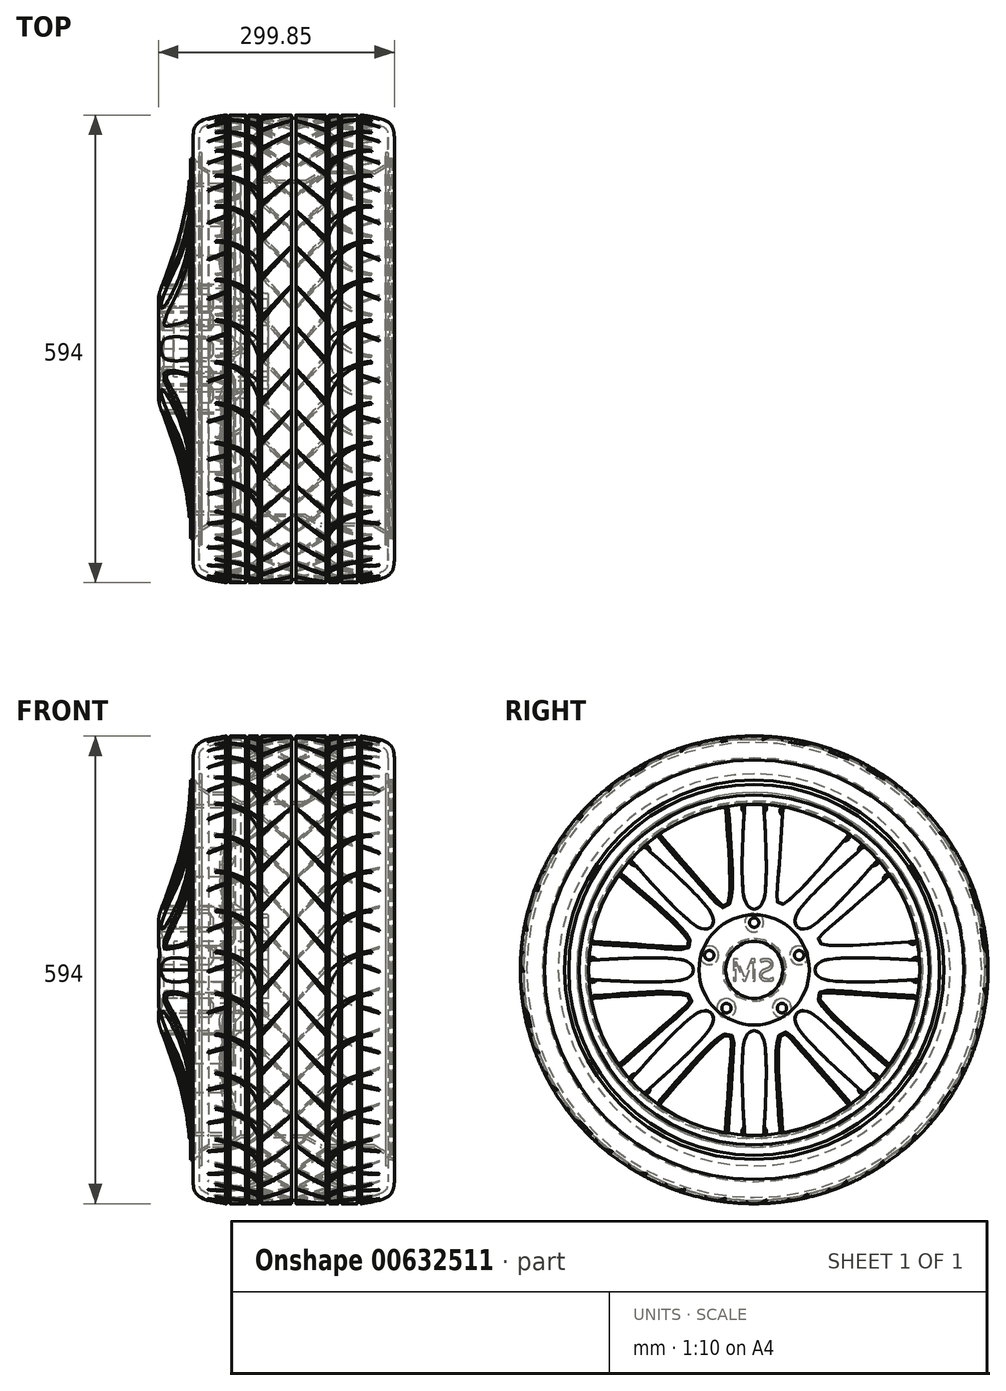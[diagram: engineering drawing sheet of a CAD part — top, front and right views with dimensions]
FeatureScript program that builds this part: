
annotation { "Feature Type Name" : "Feature", "Feature Type Description" : "" }
export const myFeature = defineFeature(function(context is Context, id is Id, definition is map)
    precondition{}
    {
        {
            var Q0;
            Q0=qCreatedBy(makeId("Front.planeOp"),FACE);
            var sketch = newSketch(context, id + "F0", { "sketchPlane" : qUnion([Q0])});
            skLineSegment(sketch, "E0", {"start": v(-128, 244.95) * mm, "end": v(-128, 266.43) * mm});
            skLineSegment(sketch, "E1", {"start": v(0, 297) * mm, "end": v(86.47, 297) * mm});
            skLineSegment(sketch, "E2", {"start": v(128, 266.43) * mm, "end": v(128, 244.95) * mm});
            skLineSegment(sketch, "E3", {"start": v(120, 249) * mm, "end": v(117, 249) * mm});
            skLineSegment(sketch, "E4", {"start": v(117, 249) * mm, "end": v(117, 241) * mm});
            skLineSegment(sketch, "E5", {"start": v(-120, 269) * mm, "end": v(-120, 249) * mm});
            skLineSegment(sketch, "E6", {"start": v(-120, 249) * mm, "end": v(-117, 249) * mm});
            skLineSegment(sketch, "E7", {"start": v(-117, 249) * mm, "end": v(-117, 241) * mm});
            skLineSegment(sketch, "E8", {"start": v(-128, 0) * mm, "end": v(128, 0) * mm});
            skArc(sketch, "E9", {"start": v(-125, 241) * mm, "mid": v(-121, 237) * mm, "end": v(-117, 241) * mm});
            skArc(sketch, "E10", {"start": v(117, 241) * mm, "mid": v(121, 237) * mm, "end": v(125, 241) * mm});
            skLineSegment(sketch, "E11", {"start": v(0, 297) * mm, "end": v(0, 289) * mm, "construction": true});
            skArc(sketch, "E12", {"start": v(-128, 244.95) * mm, "mid": v(-127.16, 242.47) * mm, "end": v(-125, 241) * mm});
            skArc(sketch, "E13", {"start": v(125, 241) * mm, "mid": v(127.16, 242.47) * mm, "end": v(128, 244.95) * mm});
            skFitSpline(sketch, "E14", {"points": [v(120, 269) * mm, v(117.14, 279.65) * mm, v(100, 286.7) * mm, v(86.47, 289) * mm], "startDerivative": vector(-1.21, 39.82) * mm, "endDerivative": vector(-44.37, 2.92) * mm});
            skFitSpline(sketch, "E15", {"points": [v(128, 266.43) * mm, v(124.6, 283.17) * mm, v(112.1, 291.85) * mm, v(98.12, 295.03) * mm, v(86.47, 297) * mm], "startDerivative": vector(-3.17, 67.96) * mm, "endDerivative": vector(-50.63, 8.67) * mm});
            skPoint(sketch, "E16.orphan", {"position": v(128, 297) * mm});
            skLineSegment(sketch, "E17.trimOffspring", {"start": v(120, 269) * mm, "end": v(120, 249) * mm});
            skFitSpline(sketch, "E18.MirrorCS", {"points": [v(-120, 269) * mm, v(-117.14, 279.65) * mm, v(-100, 286.7) * mm, v(-86.47, 289) * mm], "startDerivative": vector(1.21, 39.82) * mm, "endDerivative": vector(44.37, 2.92) * mm});
            skFitSpline(sketch, "E19.MirrorCS", {"points": [v(-128, 266.43) * mm, v(-124.6, 283.17) * mm, v(-112.1, 291.85) * mm, v(-98.12, 295.03) * mm, v(-86.47, 297) * mm], "startDerivative": vector(3.17, 67.96) * mm, "endDerivative": vector(50.63, 8.67) * mm});
            skPoint(sketch, "E20.orphan", {"position": v(-128, 297) * mm});
            skLineSegment(sketch, "E21.trimOffspring", {"start": v(-86.47, 289) * mm, "end": v(86.47, 289) * mm});
            skLineSegment(sketch, "E22", {"start": v(0, 297) * mm, "end": v(-86.47, 297) * mm});
            skSolve(sketch);
        }
        {
            var Q0;
            Q0=makeQuery(id+"F0.imprint","IMPRINT",FACE,{"disambiguationData":[TD([[makeQuery(id+"F0.imprint","IMPRINT",EDGE,{"derivedFrom":sQuery(id+"F0.wireOp",EDGE,"E0")}),-1.0]])]});
            var Q1;
            Q1=sQuery(id+"F0.wireOp",EDGE,"E8");
            revolve(context, id + "F1", {"entities" : qUnion([Q0]), "axis" : qUnion([Q1]), "revolveType" : RevolveType.FULL});
        }
        {
            var Q0;
            Q0=qCreatedBy(makeId("Front.planeOp"),FACE);
            var sketch = newSketch(context, id + "F2", { "sketchPlane" : qUnion([Q0])});
            skLineSegment(sketch, "E23.0", {"start": v(0, 297) * mm, "end": v(3, 297) * mm});
            skLineSegment(sketch, "E24.bottom", {"start": v(85, 297) * mm, "end": v(81, 297) * mm});
            skLineSegment(sketch, "E24.top", {"start": v(85, 293) * mm, "end": v(81, 293) * mm});
            skLineSegment(sketch, "E24.left", {"start": v(85, 297) * mm, "end": v(85, 293) * mm});
            skLineSegment(sketch, "E24.right", {"start": v(81, 297) * mm, "end": v(81, 293) * mm});
            skLineSegment(sketch, "E25.bottom", {"start": v(61, 297) * mm, "end": v(57, 297) * mm});
            skLineSegment(sketch, "E25.top", {"start": v(61, 293) * mm, "end": v(57, 293) * mm});
            skLineSegment(sketch, "E25.left", {"start": v(61, 297) * mm, "end": v(61, 293) * mm});
            skLineSegment(sketch, "E25.right", {"start": v(57, 297) * mm, "end": v(57, 293) * mm});
            skLineSegment(sketch, "E26.bottom", {"start": v(3, 297) * mm, "end": v(-3, 297) * mm});
            skLineSegment(sketch, "E26.top", {"start": v(3, 293) * mm, "end": v(-3, 293) * mm});
            skLineSegment(sketch, "E26.left", {"start": v(3, 297) * mm, "end": v(3, 293) * mm});
            skLineSegment(sketch, "E26.right", {"start": v(-3, 297) * mm, "end": v(-3, 293) * mm});
            skLineSegment(sketch, "E27.bottom", {"start": v(45, 297) * mm, "end": v(41, 297) * mm});
            skLineSegment(sketch, "E27.top", {"start": v(45, 293) * mm, "end": v(41, 293) * mm});
            skLineSegment(sketch, "E27.left", {"start": v(45, 297) * mm, "end": v(45, 293) * mm});
            skLineSegment(sketch, "E27.right", {"start": v(41, 297) * mm, "end": v(41, 293) * mm});
            skLineSegment(sketch, "E28.MirrorCS", {"start": v(-41, 297) * mm, "end": v(-41, 293) * mm});
            skLineSegment(sketch, "E29.MirrorCS", {"start": v(-45, 293) * mm, "end": v(-41, 293) * mm});
            skLineSegment(sketch, "E30.MirrorCS", {"start": v(-45, 297) * mm, "end": v(-45, 293) * mm});
            skLineSegment(sketch, "E31.MirrorCS", {"start": v(-57, 297) * mm, "end": v(-57, 293) * mm});
            skLineSegment(sketch, "E32.MirrorCS", {"start": v(-61, 293) * mm, "end": v(-57, 293) * mm});
            skLineSegment(sketch, "E33.MirrorCS", {"start": v(-61, 297) * mm, "end": v(-61, 293) * mm});
            skLineSegment(sketch, "E34.MirrorCS", {"start": v(-81, 297) * mm, "end": v(-81, 293) * mm});
            skLineSegment(sketch, "E35.MirrorCS", {"start": v(-85, 293) * mm, "end": v(-81, 293) * mm});
            skLineSegment(sketch, "E36.MirrorCS", {"start": v(-85, 297) * mm, "end": v(-85, 293) * mm});
            skLineSegment(sketch, "E37.MirrorCS", {"start": v(-45, 297) * mm, "end": v(-41, 297) * mm});
            skLineSegment(sketch, "E38.MirrorCS", {"start": v(-61, 297) * mm, "end": v(-57, 297) * mm});
            skLineSegment(sketch, "E39.MirrorCS", {"start": v(-85, 297) * mm, "end": v(-81, 297) * mm});
            skLineSegment(sketch, "E40.trimOffspring", {"start": v(41, 297) * mm, "end": v(45, 297) * mm});
            skLineSegment(sketch, "E41.trimOffspring", {"start": v(57, 297) * mm, "end": v(61, 297) * mm});
            skLineSegment(sketch, "E42.trimOffspring", {"start": v(81, 297) * mm, "end": v(85, 297) * mm});
            skPoint(sketch, "E43.orphan", {"position": v(86.47, 297) * mm});
            skSolve(sketch);
        }
        {
            var Q0;
            Q0=qSketchRegion(id+"F2",true);
            var Q1;
            Q1=sQuery(id+"F0.wireOp",EDGE,"E8");
            revolve(context, id + "F3", {"operationType" : NewBodyOperationType.REMOVE, "entities" : qUnion([Q0]), "axis" : qUnion([Q1]), "revolveType" : RevolveType.FULL, "oppositeDirection" : true});
        }
        {
            var Q0;
            Q0=sQuery(id+"F0.wireOp",VERTEX,"E22.start");
            var Q1;
            Q1=sQuery(id+"F0.wireOp",EDGE,"E11");
            cPlane(context, id + "F4", {"entities" : qUnion([Q0, Q1]), "cplaneType" : CPlaneType.CURVE_POINT, "offset" : 5 * mm, "width" : 150 * mm, "height" : 150 * mm});
        }
        {
            var Q0;
            Q0=qCreatedBy(id+"F4.planeOp",FACE);
            var sketch = newSketch(context, id + "F5", { "sketchPlane" : qUnion([Q0])});
            skPoint(sketch, "E44.0", {"position": v(0, 0) * mm});
            skLineSegment(sketch, "E45", {"start": v(-41, 12.66) * mm, "end": v(-3, -28.5) * mm});
            skLineSegment(sketch, "E46", {"start": v(-41, 18.65) * mm, "end": v(-3, -26.48) * mm});
            skLineSegment(sketch, "E47", {"start": v(0, 0) * mm, "end": v(0, 30) * mm, "construction": true});
            skLineSegment(sketch, "E48.MirrorCS", {"start": v(41, 12.66) * mm, "end": v(3, -28.5) * mm});
            skLineSegment(sketch, "E49.MirrorCS", {"start": v(41, 18.65) * mm, "end": v(3, -26.48) * mm});
            skLineSegment(sketch, "E50", {"start": v(-41, 18.65) * mm, "end": v(-41, 12.66) * mm});
            skLineSegment(sketch, "E51", {"start": v(-3, -28.5) * mm, "end": v(-3, -26.48) * mm});
            skLineSegment(sketch, "E52", {"start": v(3, -26.48) * mm, "end": v(3, -28.5) * mm});
            skLineSegment(sketch, "E53", {"start": v(41, 18.65) * mm, "end": v(41, 12.66) * mm});
            skArc(sketch, "E54", {"start": v(45, -11.11) * mm, "mid": v(74.04, -31.51) * mm, "end": v(109.1, -37) * mm});
            skArc(sketch, "E55", {"start": v(45, 8.9) * mm, "mid": v(69.14, -24.55) * mm, "end": v(109.1, -34.84) * mm});
            skLineSegment(sketch, "E56", {"start": v(109.1, -37) * mm, "end": v(109.1, -34.84) * mm});
            skLineSegment(sketch, "E57", {"start": v(45, -11.11) * mm, "end": v(45, 8.9) * mm});
            skLineSegment(sketch, "E58.MirrorCS", {"start": v(-109.1, -37) * mm, "end": v(-109.1, -34.84) * mm});
            skArc(sketch, "E59.MirrorCS", {"start": v(-45, -11.11) * mm, "mid": v(-74.04, -31.51) * mm, "end": v(-109.1, -37) * mm});
            skLineSegment(sketch, "E60.MirrorCS", {"start": v(-45, -11.11) * mm, "end": v(-45, 8.9) * mm});
            skArc(sketch, "E61.MirrorCS", {"start": v(-45, 8.9) * mm, "mid": v(-69.14, -24.55) * mm, "end": v(-109.1, -34.84) * mm});
            skLineSegment(sketch, "E62", {"start": v(85, -18.42) * mm, "end": v(108.99, -9.9) * mm});
            skLineSegment(sketch, "E63", {"start": v(85, -20.44) * mm, "end": v(108.99, -11.92) * mm});
            skLineSegment(sketch, "E64", {"start": v(108.99, -11.92) * mm, "end": v(108.99, -9.9) * mm});
            skLineSegment(sketch, "E65", {"start": v(85, -20.44) * mm, "end": v(85, -18.42) * mm});
            skLineSegment(sketch, "E66.MirrorCS", {"start": v(-85, -20.44) * mm, "end": v(-85, -18.42) * mm});
            skLineSegment(sketch, "E67.MirrorCS", {"start": v(-108.99, -11.92) * mm, "end": v(-108.99, -9.9) * mm});
            skLineSegment(sketch, "E68.MirrorCS", {"start": v(-85, -20.44) * mm, "end": v(-108.99, -11.92) * mm});
            skLineSegment(sketch, "E69.MirrorCS", {"start": v(-85, -18.42) * mm, "end": v(-108.99, -9.9) * mm});
            skSolve(sketch);
        }
        {
            var Q0;
            Q0=qSketchRegion(id+"F5",true);
            extrude(context, id + "F6", {"entities" : qUnion([Q0]), "depth" : 4.3 * mm});
        }
        {
            var Q0;
            Q0=makeQuery(id+"F6.opExtrude","SWEPT_BODY",BODY,{"disambiguationData":[OSD([sQuery(id+"F5.wireOp",EDGE,"E45"),sQuery(id+"F5.wireOp",EDGE,"E46"),sQuery(id+"F5.wireOp",EDGE,"E50"),sQuery(id+"F5.wireOp",EDGE,"E51")])]});
            var Q1;
            Q1=makeQuery(id+"F6.opExtrude","SWEPT_BODY",BODY,{"disambiguationData":[OSD([sQuery(id+"F5.wireOp",EDGE,"E48.MirrorCS"),sQuery(id+"F5.wireOp",EDGE,"E49.MirrorCS"),sQuery(id+"F5.wireOp",EDGE,"E52"),sQuery(id+"F5.wireOp",EDGE,"E53")])]});
            var Q2;
            Q2=makeQuery(id+"F6.opExtrude","SWEPT_BODY",BODY,{"disambiguationData":[OSD([sQuery(id+"F5.wireOp",EDGE,"E54"),sQuery(id+"F5.wireOp",EDGE,"E55"),sQuery(id+"F5.wireOp",EDGE,"E56"),sQuery(id+"F5.wireOp",EDGE,"E57")])]});
            var Q3;
            Q3=makeQuery(id+"F6.opExtrude","SWEPT_BODY",BODY,{"disambiguationData":[OSD([sQuery(id+"F5.wireOp",EDGE,"E58.MirrorCS"),sQuery(id+"F5.wireOp",EDGE,"E59.MirrorCS"),sQuery(id+"F5.wireOp",EDGE,"E60.MirrorCS"),sQuery(id+"F5.wireOp",EDGE,"E61.MirrorCS")])]});
            var Q4;
            Q4=makeQuery(id+"F6.opExtrude","SWEPT_BODY",BODY,{"disambiguationData":[OSD([sQuery(id+"F5.wireOp",EDGE,"E62"),sQuery(id+"F5.wireOp",EDGE,"E63"),sQuery(id+"F5.wireOp",EDGE,"E64"),sQuery(id+"F5.wireOp",EDGE,"E65")])]});
            var Q5;
            Q5=makeQuery(id+"F6.opExtrude","SWEPT_BODY",BODY,{"disambiguationData":[OSD([sQuery(id+"F5.wireOp",EDGE,"E66.MirrorCS"),sQuery(id+"F5.wireOp",EDGE,"E67.MirrorCS"),sQuery(id+"F5.wireOp",EDGE,"E68.MirrorCS"),sQuery(id+"F5.wireOp",EDGE,"E69.MirrorCS")])]});
            var Q6;
            Q6=sQuery(id+"F0.wireOp",EDGE,"E8");
            circularPattern(context, id + "F7", {"operationType" : NewBodyOperationType.REMOVE, "entities" : qUnion([Q0, Q1, Q2, Q3, Q4, Q5]), "axis" : qUnion([Q6]), "angle" : 360 * degree, "instanceCount" : round(35), "equalSpace" : true});
        }
        {
            var Q0;
            Q0=qCreatedBy(makeId("Front.planeOp"),FACE);
            var sketch = newSketch(context, id + "F8", { "sketchPlane" : qUnion([Q0])});
            skLineSegment(sketch, "E70", {"start": v(-170.5, 0) * mm, "end": v(125, 0) * mm});
            skLineSegment(sketch, "E71", {"start": v(-152.5, 0) * mm, "end": v(-152.5, 36.25) * mm});
            skLineSegment(sketch, "E72", {"start": v(-152.5, 36.25) * mm, "end": v(-32.5, 36.25) * mm});
            skLineSegment(sketch, "E73", {"start": v(-32.5, 36.25) * mm, "end": v(-32.5, 70) * mm});
            skLineSegment(sketch, "E74", {"start": v(102.02, 222.3) * mm, "end": v(125, 235.57) * mm});
            skLineSegment(sketch, "E75", {"start": v(125, 235.57) * mm, "end": v(125, 241.3) * mm});
            skLineSegment(sketch, "E76", {"start": v(125, 241.3) * mm, "end": v(122, 241.3) * mm});
            skLineSegment(sketch, "E77", {"start": v(102.02, 222.3) * mm, "end": v(35.16, 222.3) * mm});
            skLineSegment(sketch, "E78", {"start": v(35.16, 222.3) * mm, "end": v(14.37, 210.3) * mm});
            skLineSegment(sketch, "E79", {"start": v(14.37, 210.3) * mm, "end": v(-67.23, 210.3) * mm});
            skLineSegment(sketch, "E80", {"start": v(-67.23, 210.3) * mm, "end": v(-88.02, 222.3) * mm});
            skLineSegment(sketch, "E81", {"start": v(-88.02, 222.3) * mm, "end": v(-108.02, 222.3) * mm});
            skLineSegment(sketch, "E82", {"start": v(-108.02, 222.3) * mm, "end": v(-131, 235.57) * mm});
            skLineSegment(sketch, "E83", {"start": v(-131, 235.57) * mm, "end": v(-131, 241.3) * mm});
            skLineSegment(sketch, "E84", {"start": v(-131, 241.3) * mm, "end": v(-128, 241.3) * mm});
            skLineSegment(sketch, "E85.0", {"start": v(122, 237.3) * mm, "end": v(122, 241.3) * mm});
            skLineSegment(sketch, "E85.1", {"start": v(101.22, 225.3) * mm, "end": v(122, 237.3) * mm});
            skLineSegment(sketch, "E85.2", {"start": v(101.22, 225.3) * mm, "end": v(34.35, 225.3) * mm});
            skLineSegment(sketch, "E85.3", {"start": v(34.35, 225.3) * mm, "end": v(13.57, 213.3) * mm});
            skLineSegment(sketch, "E85.4", {"start": v(13.57, 213.3) * mm, "end": v(-66.43, 213.3) * mm});
            skLineSegment(sketch, "E85.5", {"start": v(-128, 237.3) * mm, "end": v(-128, 241.3) * mm});
            skLineSegment(sketch, "E85.6", {"start": v(-107.22, 225.3) * mm, "end": v(-128, 237.3) * mm});
            skLineSegment(sketch, "E85.7", {"start": v(-87.22, 225.3) * mm, "end": v(-107.22, 225.3) * mm});
            skLineSegment(sketch, "E85.8", {"start": v(-66.43, 213.3) * mm, "end": v(-87.22, 225.3) * mm});
            skLineSegment(sketch, "E86", {"start": v(-170.5, 0) * mm, "end": v(-170.5, 37.49) * mm});
            skFitSpline(sketch, "E87", {"points": [v(-165.54, 39.55) * mm, v(-168.06, 48.15) * mm, v(-171.62, 59.11) * mm, v(-169.25, 74.67) * mm, v(-148.34, 134.05) * mm, v(-134.39, 196.84) * mm, v(-131, 235.57) * mm], "startDerivative": vector(-23.26, 90.7) * mm, "endDerivative": vector(11.52, 191.45) * mm});
            skFitSpline(sketch, "E88", {"points": [v(-32.5, 70) * mm, v(-65.4, 77.45) * mm, v(-85.25, 101.16) * mm, v(-90.29, 133.45) * mm, v(-80.8, 197.46) * mm, v(-74.43, 214.45) * mm], "startDerivative": vector(-178.56, 14.97) * mm, "endDerivative": vector(43.2, 91.04) * mm});
            skArc(sketch, "E89", {"start": v(-165.54, 39.55) * mm, "mid": v(-168.7, 40.17) * mm, "end": v(-170.5, 37.49) * mm});
            skLineSegment(sketch, "E90", {"start": v(-107.22, 225.3) * mm, "end": v(-108.02, 255.3) * mm, "construction": true});
            skLineSegment(sketch, "E91", {"start": v(-108.02, 255.3) * mm, "end": v(101.22, 255.3) * mm, "construction": true});
            skLineSegment(sketch, "E92", {"start": v(101.22, 255.3) * mm, "end": v(101.22, 225.3) * mm, "construction": true});
            skPoint(sketch, "E93", {"position": v(-3.4, 255.3) * mm});
            skSolve(sketch);
        }
        {
            var Q0;
            {var subQ2=sQuery(id+"F8.wireOp",EDGE,"E71");Q0=makeQuery(id+"F8.imprint","IMPRINT",FACE,{"disambiguationData":[TD([[makeQuery(id+"F8.imprint","IMPRINT",EDGE,{"derivedFrom":subQ2}),1.0]])]});}
            var Q1;
            Q1=sQuery(id+"F8.wireOp",EDGE,"E70");
            revolve(context, id + "F9", {"entities" : qUnion([Q0]), "axis" : qUnion([Q1]), "revolveType" : RevolveType.FULL});
        }
        {
            var Q0;
            Q0=makeQuery(id+"F8.imprint","IMPRINT",FACE,{"disambiguationData":[TD([[makeQuery(id+"F8.imprint","IMPRINT",EDGE,{"derivedFrom":sQuery(id+"F8.wireOp",EDGE,"E74")}),1.0]])]});
            var Q1;
            Q1=sQuery(id+"F8.wireOp",EDGE,"E70");
            revolve(context, id + "F10", {"entities" : qUnion([Q0]), "axis" : qUnion([Q1]), "revolveType" : RevolveType.FULL});
        }
        {
            var Q0;
            Q0=makeQuery(id+"F9.opRevolve","SWEPT_FACE",FACE,{"disambiguationData":[OSD([sQuery(id+"F8.wireOp",EDGE,"E73")])]});
            var sketch = newSketch(context, id + "F11", { "sketchPlane" : qUnion([Q0])});
            skCircle(sketch, "E94", {"center": v(0, 60) * mm, "radius": 6 * mm});
            skPoint(sketch, "E95.0", {"position": v(0, 0) * mm});
            skCircle(sketch, "E96.1.0", {"center": v(-57.06, 18.54) * mm, "radius": 6 * mm});
            skCircle(sketch, "E96.2.0", {"center": v(-35.27, -48.54) * mm, "radius": 6 * mm});
            skCircle(sketch, "E97.0.3.0", {"center": v(35.27, -48.54) * mm, "radius": 6 * mm});
            skCircle(sketch, "E97.0.4.0", {"center": v(57.06, 18.54) * mm, "radius": 6 * mm});
            skPoint(sketch, "E98.0", {"position": v(0, 210.3) * mm});
            skArc(sketch, "E99", {"start": v(12.06, 209.95) * mm, "mid": v(0, 210.3) * mm, "end": v(-12.06, 209.95) * mm});
            skFitSpline(sketch, "E100", {"points": [v(-12.06, 209.95) * mm, v(-15.11, 148.8) * mm, v(-14.17, 100.77) * mm, v(-9.46, 83.19) * mm, v(0, 77) * mm], "startDerivative": vector(-11.14, -175.96) * mm, "endDerivative": vector(83.69, -7.97) * mm});
            skLineSegment(sketch, "E101", {"start": v(0, 60) * mm, "end": v(0, 77) * mm, "construction": true});
            skFitSpline(sketch, "E102", {"points": [v(36.64, 207.08) * mm, v(29.5, 101.83) * mm, v(32.97, 82.07) * mm, v(98.48, 146.54) * mm, v(120.7, 172.21) * mm], "startDerivative": vector(-23.36, -349.3) * mm, "endDerivative": vector(82.69, 95.15) * mm});
            skArc(sketch, "E103.trimOffspring", {"start": v(120.7, 172.21) * mm, "mid": v(80.58, 194.25) * mm, "end": v(36.64, 207.08) * mm});
            skFitSpline(sketch, "E104.MirrorCS", {"points": [v(12.06, 209.95) * mm, v(15.11, 148.8) * mm, v(14.17, 100.77) * mm, v(9.46, 83.19) * mm, v(0, 77) * mm], "startDerivative": vector(11.14, -175.96) * mm, "endDerivative": vector(-83.69, -7.97) * mm});
            skSolve(sketch);
        }
        {
            var Q0;
            Q0=makeQuery(id+"F11.imprint","IMPRINT",FACE,{"disambiguationData":[TD([[makeQuery(id+"F11.imprint","IMPRINT",EDGE,{"derivedFrom":sQuery(id+"F11.wireOp",EDGE,"E99")}),1.0]])]});
            var Q1;
            Q1=makeQuery(id+"F11.imprint","IMPRINT",FACE,{"disambiguationData":[TD([[makeQuery(id+"F11.imprint","IMPRINT",EDGE,{"derivedFrom":sQuery(id+"F11.wireOp",EDGE,"E102")}),1.0]])]});
            var Q2;
            Q2=makeQuery(id+"F9.opRevolve","SWEPT_BODY",BODY,{"disambiguationData":[OSD([sQuery(id+"F8.wireOp",EDGE,"E70"),sQuery(id+"F8.wireOp",EDGE,"E71"),sQuery(id+"F8.wireOp",EDGE,"E72"),sQuery(id+"F8.wireOp",EDGE,"E73"),sQuery(id+"F8.wireOp",EDGE,"E80"),sQuery(id+"F8.wireOp",EDGE,"E81"),sQuery(id+"F8.wireOp",EDGE,"E82"),sQuery(id+"F8.wireOp",EDGE,"E86"),sQuery(id+"F8.wireOp",EDGE,"E87"),sQuery(id+"F8.wireOp",EDGE,"E88"),sQuery(id+"F8.wireOp",EDGE,"E89")])]});
            extrude(context, id + "F12", {"entities" : qUnion([Q0, Q1]), "oppositeDirection" : true, "endBoundEntityBody" : qUnion([Q2]), "depth" : 150 * mm});
        }
        {
            var Q0;
            Q0=makeQuery(id+"F12.opExtrude","SWEPT_BODY",BODY,{"disambiguationData":[OSD([sQuery(id+"F11.wireOp",EDGE,"E99"),sQuery(id+"F11.wireOp",EDGE,"E100"),sQuery(id+"F11.wireOp",EDGE,"E104.MirrorCS")])]});
            var Q1;
            Q1=makeQuery(id+"F12.opExtrude","SWEPT_BODY",BODY,{"disambiguationData":[OSD([sQuery(id+"F11.wireOp",EDGE,"E102"),sQuery(id+"F11.wireOp",EDGE,"E103.trimOffspring")])]});
            var Q2;
            Q2=sQuery(id+"F8.wireOp",EDGE,"E70");
            circularPattern(context, id + "F13", {"operationType" : NewBodyOperationType.REMOVE, "entities" : qUnion([Q0, Q1]), "axis" : qUnion([Q2]), "angle" : 360 * degree, "instanceCount" : round(8), "equalSpace" : true});
        }
        {
            var Q0;
            Q0=makeQuery(id+"F11.imprint","IMPRINT",FACE,{"disambiguationData":[TD([[makeQuery(id+"F11.imprint","IMPRINT",EDGE,{"derivedFrom":sQuery(id+"F11.wireOp",EDGE,"E94")}),-1.0]])]});
            cPlane(context, id + "F14", {"entities" : qUnion([Q0]), "cplaneType" : CPlaneType.OFFSET, "offset" : 150 * mm, "oppositeDirection" : true, "width" : 150 * mm, "height" : 150 * mm});
        }
        {
            var Q0;
            Q0=qCreatedBy(id+"F14.planeOp",FACE);
            var sketch = newSketch(context, id + "F15", { "sketchPlane" : qUnion([Q0])});
            skPoint(sketch, "E105.0", {"position": v(-35.27, -48.54) * mm});
            skPoint(sketch, "E105.1", {"position": v(-57.06, 18.54) * mm});
            skPoint(sketch, "E105.2", {"position": v(0, 60) * mm});
            skPoint(sketch, "E105.3", {"position": v(57.06, 18.54) * mm});
            skPoint(sketch, "E105.4", {"position": v(35.27, -48.54) * mm});
            skSolve(sketch);
        }
        {
            var Q0;
            Q0=sQuery(id+"F15.wireOp",VERTEX,"E105.3");
            var Q1;
            Q1=sQuery(id+"F15.wireOp",VERTEX,"E105.4");
            var Q2;
            Q2=sQuery(id+"F15.wireOp",VERTEX,"E105.0");
            var Q3;
            Q3=sQuery(id+"F15.wireOp",VERTEX,"E105.1");
            var Q4;
            Q4=sQuery(id+"F15.wireOp",VERTEX,"E105.2");
            var Q5;
            Q5=makeQuery(id+"F9.opRevolve","SWEPT_BODY",BODY,{"disambiguationData":[OSD([sQuery(id+"F8.wireOp",EDGE,"E70"),sQuery(id+"F8.wireOp",EDGE,"E71"),sQuery(id+"F8.wireOp",EDGE,"E72"),sQuery(id+"F8.wireOp",EDGE,"E73"),sQuery(id+"F8.wireOp",EDGE,"E80"),sQuery(id+"F8.wireOp",EDGE,"E81"),sQuery(id+"F8.wireOp",EDGE,"E82"),sQuery(id+"F8.wireOp",EDGE,"E86"),sQuery(id+"F8.wireOp",EDGE,"E87"),sQuery(id+"F8.wireOp",EDGE,"E88"),sQuery(id+"F8.wireOp",EDGE,"E89")])]});
            hole(context, id + "F16", {"style" : HoleStyle.SIMPLE, "holeDiameter" : 24 * mm, "endStyle" : HoleEndStyle.BLIND, "oppositeDirection" : true, "holeDepth" : 62 * mm, "locations" : qUnion([Q0, Q1, Q2, Q3, Q4]), "scope" : qUnion([Q5])});
        }
        {
            var Q0;
            Q0=sQuery(id+"F15.wireOp",VERTEX,"E105.4");
            var Q1;
            Q1=sQuery(id+"F15.wireOp",VERTEX,"E105.0");
            var Q2;
            Q2=sQuery(id+"F15.wireOp",VERTEX,"E105.1");
            var Q3;
            Q3=sQuery(id+"F15.wireOp",VERTEX,"E105.3");
            var Q4;
            Q4=sQuery(id+"F15.wireOp",VERTEX,"E105.2");
            var Q5;
            Q5=makeQuery(id+"F9.opRevolve","SWEPT_BODY",BODY,{"disambiguationData":[OSD([sQuery(id+"F8.wireOp",EDGE,"E70"),sQuery(id+"F8.wireOp",EDGE,"E71"),sQuery(id+"F8.wireOp",EDGE,"E72"),sQuery(id+"F8.wireOp",EDGE,"E73"),sQuery(id+"F8.wireOp",EDGE,"E80"),sQuery(id+"F8.wireOp",EDGE,"E81"),sQuery(id+"F8.wireOp",EDGE,"E82"),sQuery(id+"F8.wireOp",EDGE,"E86"),sQuery(id+"F8.wireOp",EDGE,"E87"),sQuery(id+"F8.wireOp",EDGE,"E88"),sQuery(id+"F8.wireOp",EDGE,"E89")])]});
            hole(context, id + "F17", {"style" : HoleStyle.C_SINK, "holeDiameter" : 12 * mm, "cSinkDiameter" : 24 * mm, "endStyle" : HoleEndStyle.THROUGH, "oppositeDirection" : true, "locations" : qUnion([Q0, Q1, Q2, Q3, Q4]), "scope" : qUnion([Q5]), "cSinkAngle" : 90 * degree});
        }
        {
            var Q0;
            Q0=makeQuery(id+"F13.boolean.opBoolean","COPY",FACE,{"derivedFrom":makeQuery(id+"F13.opPattern","COPY",FACE,{"derivedFrom":makeQuery(id+"F12.opExtrude","SWEPT_FACE",FACE,{"disambiguationData":[OSD([sQuery(id+"F11.wireOp",EDGE,"E102")])]}),"instanceName":"1"})});
            var Q1;
            Q1=makeQuery(id+"F13.boolean.opBoolean","COPY",FACE,{"derivedFrom":makeQuery(id+"F13.opPattern","COPY",FACE,{"derivedFrom":makeQuery(id+"F12.opExtrude","SWEPT_FACE",FACE,{"disambiguationData":[OSD([sQuery(id+"F11.wireOp",EDGE,"E102")])]}),"instanceName":"2"})});
            var Q2;
            Q2=makeQuery(id+"F13.boolean.opBoolean","COPY",FACE,{"derivedFrom":makeQuery(id+"F13.opPattern","COPY",FACE,{"derivedFrom":makeQuery(id+"F12.opExtrude","SWEPT_FACE",FACE,{"disambiguationData":[OSD([sQuery(id+"F11.wireOp",EDGE,"E102")])]}),"instanceName":"4"})});
            var Q3;
            Q3=makeQuery(id+"F13.boolean.opBoolean","COPY",FACE,{"derivedFrom":makeQuery(id+"F13.opPattern","COPY",FACE,{"derivedFrom":makeQuery(id+"F12.opExtrude","SWEPT_FACE",FACE,{"disambiguationData":[OSD([sQuery(id+"F11.wireOp",EDGE,"E102")])]}),"instanceName":"5"})});
            var Q4;
            Q4=makeQuery(id+"F13.boolean.opBoolean","COPY",FACE,{"derivedFrom":makeQuery(id+"F13.opPattern","COPY",FACE,{"derivedFrom":makeQuery(id+"F12.opExtrude","SWEPT_FACE",FACE,{"disambiguationData":[OSD([sQuery(id+"F11.wireOp",EDGE,"E102")])]}),"instanceName":"6"})});
            var Q5;
            Q5=makeQuery(id+"F13.boolean.opBoolean","COPY",FACE,{"derivedFrom":makeQuery(id+"F13.opPattern","COPY",FACE,{"derivedFrom":makeQuery(id+"F12.opExtrude","SWEPT_FACE",FACE,{"disambiguationData":[OSD([sQuery(id+"F11.wireOp",EDGE,"E103.trimOffspring")])]}),"instanceName":"7"})});
            var Q6;
            Q6=makeQuery(id+"F13.boolean.opBoolean","COPY",FACE,{"derivedFrom":makeQuery(id+"F13.opPattern","COPY",FACE,{"derivedFrom":makeQuery(id+"F12.opExtrude","SWEPT_FACE",FACE,{"disambiguationData":[OSD([sQuery(id+"F11.wireOp",EDGE,"E99")])]}),"instanceName":"7"})});
            var Q7;
            Q7=makeQuery(id+"F13.boolean.opBoolean","COPY",FACE,{"derivedFrom":makeQuery(id+"F12.opExtrude","SWEPT_FACE",FACE,{"disambiguationData":[OSD([sQuery(id+"F11.wireOp",EDGE,"E103.trimOffspring")])]})});
            var Q8;
            Q8=makeQuery(id+"F13.boolean.opBoolean","COPY",FACE,{"derivedFrom":makeQuery(id+"F12.opExtrude","SWEPT_FACE",FACE,{"disambiguationData":[OSD([sQuery(id+"F11.wireOp",EDGE,"E99")])]})});
            var Q9;
            Q9=makeQuery(id+"F13.boolean.opBoolean","COPY",FACE,{"derivedFrom":makeQuery(id+"F13.opPattern","COPY",FACE,{"derivedFrom":makeQuery(id+"F12.opExtrude","SWEPT_FACE",FACE,{"disambiguationData":[OSD([sQuery(id+"F11.wireOp",EDGE,"E99")])]}),"instanceName":"6"})});
            var Q10;
            Q10=makeQuery(id+"F13.boolean.opBoolean","COPY",FACE,{"derivedFrom":makeQuery(id+"F13.opPattern","COPY",FACE,{"derivedFrom":makeQuery(id+"F12.opExtrude","SWEPT_FACE",FACE,{"disambiguationData":[OSD([sQuery(id+"F11.wireOp",EDGE,"E99")])]}),"instanceName":"5"})});
            var Q11;
            Q11=makeQuery(id+"F13.boolean.opBoolean","COPY",FACE,{"derivedFrom":makeQuery(id+"F13.opPattern","COPY",FACE,{"derivedFrom":makeQuery(id+"F12.opExtrude","SWEPT_FACE",FACE,{"disambiguationData":[OSD([sQuery(id+"F11.wireOp",EDGE,"E99")])]}),"instanceName":"4"})});
            var Q12;
            Q12=makeQuery(id+"F13.boolean.opBoolean","COPY",FACE,{"derivedFrom":makeQuery(id+"F13.opPattern","COPY",FACE,{"derivedFrom":makeQuery(id+"F12.opExtrude","SWEPT_FACE",FACE,{"disambiguationData":[OSD([sQuery(id+"F11.wireOp",EDGE,"E99")])]}),"instanceName":"3"})});
            var Q13;
            Q13=makeQuery(id+"F13.boolean.opBoolean","COPY",FACE,{"derivedFrom":makeQuery(id+"F13.opPattern","COPY",FACE,{"derivedFrom":makeQuery(id+"F12.opExtrude","SWEPT_FACE",FACE,{"disambiguationData":[OSD([sQuery(id+"F11.wireOp",EDGE,"E99")])]}),"instanceName":"2"})});
            var Q14;
            Q14=makeQuery(id+"F13.boolean.opBoolean","COPY",FACE,{"derivedFrom":makeQuery(id+"F13.opPattern","COPY",FACE,{"derivedFrom":makeQuery(id+"F12.opExtrude","SWEPT_FACE",FACE,{"disambiguationData":[OSD([sQuery(id+"F11.wireOp",EDGE,"E99")])]}),"instanceName":"1"})});
            var Q15;
            Q15=makeQuery(id+"F13.boolean.opBoolean","COPY",FACE,{"derivedFrom":makeQuery(id+"F13.opPattern","COPY",FACE,{"derivedFrom":makeQuery(id+"F12.opExtrude","SWEPT_FACE",FACE,{"disambiguationData":[OSD([sQuery(id+"F11.wireOp",EDGE,"E102")])]}),"instanceName":"3"})});
            fillet(context, id + "F18", {"entities" : qUnion([Q0, Q1, Q2, Q3, Q4, Q5, Q6, Q7, Q8, Q9, Q10, Q11, Q12, Q13, Q14, Q15]), "radius" : 3.5 * mm, "tangentPropagation" : true, "allowEdgeOverflow" : false});
        }
        {
            var Q0;
            Q0=makeQuery(id+"F9.opRevolve","SWEPT_FACE",FACE,{"disambiguationData":[OSD([sQuery(id+"F8.wireOp",EDGE,"E86")])]});
            var sketch = newSketch(context, id + "F19", { "sketchPlane" : qUnion([Q0])});
            skText(sketch, "E106", { "text": "SM", "fontName": "OpenSans-Regular.ttf"});
            const initialGuessF19  = {"E106": [-0.02627, -0.01397, 1, 0, 0.02794]};
            skSetInitialGuess(sketch, initialGuessF19);
            skSolve(sketch);
        }
        {
            var Q0;
            Q0=qSketchRegion(id+"F19",true);
            extrude(context, id + "F20", {"entities" : qUnion([Q0]), "operationType" : NewBodyOperationType.ADD, "depth" : 1 * mm});
        }
        {
            var Q0;
            Q0=makeQuery(id+"F10.opRevolve","SWEPT_EDGE",EDGE,{"disambiguationData":[OSD([sQuery(id+"F8.wireOp",EDGE,"E85.4"),sQuery(id+"F8.wireOp",EDGE,"E85.8")])]});
            var Q1;
            Q1=makeQuery(id+"F10.opRevolve","SWEPT_EDGE",EDGE,{"disambiguationData":[OSD([sQuery(id+"F8.wireOp",EDGE,"E85.3"),sQuery(id+"F8.wireOp",EDGE,"E85.4")])]});
            var Q2;
            Q2=makeQuery(id+"F10.opRevolve","SWEPT_EDGE",EDGE,{"disambiguationData":[OSD([sQuery(id+"F8.wireOp",EDGE,"E85.2"),sQuery(id+"F8.wireOp",EDGE,"E85.3")])]});
            var Q3;
            Q3=makeQuery(id+"F10.opRevolve","SWEPT_EDGE",EDGE,{"disambiguationData":[OSD([sQuery(id+"F8.wireOp",EDGE,"E85.1"),sQuery(id+"F8.wireOp",EDGE,"E85.2")])]});
            var Q4;
            Q4=makeQuery(id+"F10.opRevolve","SWEPT_EDGE",EDGE,{"disambiguationData":[OSD([sQuery(id+"F8.wireOp",EDGE,"E85.7"),sQuery(id+"F8.wireOp",EDGE,"E85.8")])]});
            var Q5;
            Q5=makeQuery(id+"F10.opRevolve","SWEPT_EDGE",EDGE,{"disambiguationData":[OSD([sQuery(id+"F8.wireOp",EDGE,"E85.6"),sQuery(id+"F8.wireOp",EDGE,"E85.7")])]});
            var Q6;
            Q6=makeQuery(id+"F10.opRevolve","SWEPT_EDGE",EDGE,{"disambiguationData":[OSD([sQuery(id+"F8.wireOp",EDGE,"E85.0"),sQuery(id+"F8.wireOp",EDGE,"E85.1")])]});
            var Q7;
            Q7=makeQuery(id+"F10.opRevolve","SWEPT_EDGE",EDGE,{"disambiguationData":[OSD([sQuery(id+"F8.wireOp",EDGE,"E85.5"),sQuery(id+"F8.wireOp",EDGE,"E85.6")])]});
            fillet(context, id + "F21", {"entities" : qUnion([Q0, Q1, Q2, Q3, Q4, Q5, Q6, Q7]), "radius" : 3 * mm, "tangentPropagation" : true, "allowEdgeOverflow" : false});
        }
        {
            var Q0;
            Q0=makeQuery(id+"F10.opRevolve","SWEPT_EDGE",EDGE,{"disambiguationData":[OSD([sQuery(id+"F8.wireOp",EDGE,"E74"),sQuery(id+"F8.wireOp",EDGE,"E77")])]});
            var Q1;
            Q1=makeQuery(id+"F10.opRevolve","SWEPT_EDGE",EDGE,{"disambiguationData":[OSD([sQuery(id+"F8.wireOp",EDGE,"E77"),sQuery(id+"F8.wireOp",EDGE,"E78")])]});
            var Q2;
            Q2=makeQuery(id+"F10.opRevolve","SWEPT_EDGE",EDGE,{"disambiguationData":[OSD([sQuery(id+"F8.wireOp",EDGE,"E78"),sQuery(id+"F8.wireOp",EDGE,"E79")])]});
            fillet(context, id + "F22", {"entities" : qUnion([Q0, Q1, Q2]), "radius" : 3 * mm, "tangentPropagation" : true, "allowEdgeOverflow" : false});
        }
        {
            var Q0;
            Q0=makeQuery(id+"F9.opRevolve","SWEPT_EDGE",EDGE,{"disambiguationData":[OSD([sQuery(id+"F8.wireOp",EDGE,"E71"),sQuery(id+"F8.wireOp",EDGE,"E72")])]});
            fillet(context, id + "F23", {"entities" : qUnion([Q0]), "radius" : 2 * mm, "tangentPropagation" : true, "allowEdgeOverflow" : false});
        }
    });
